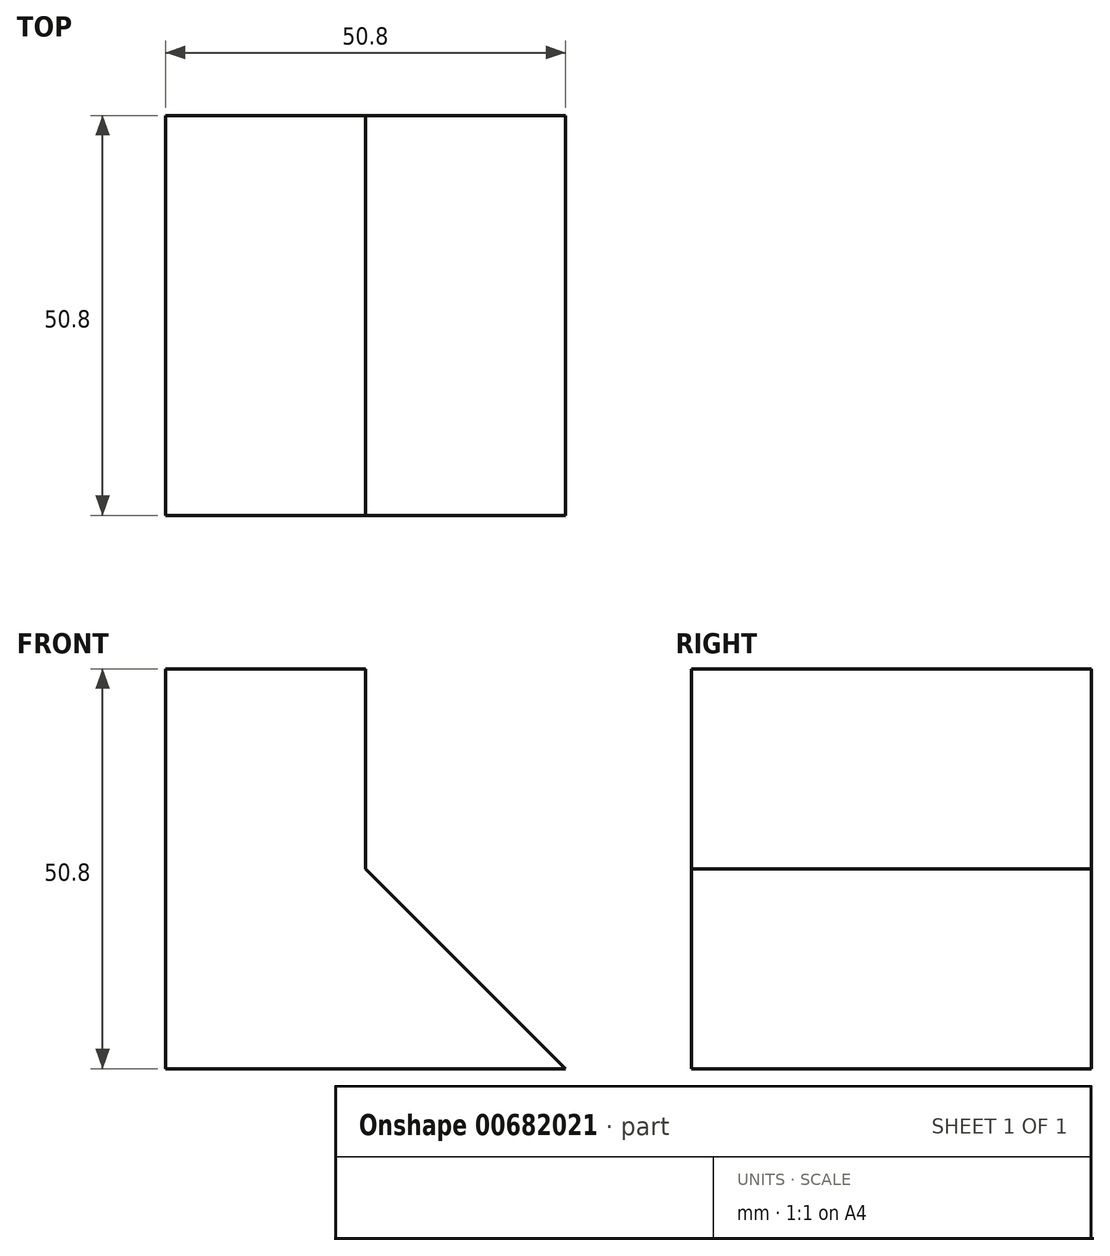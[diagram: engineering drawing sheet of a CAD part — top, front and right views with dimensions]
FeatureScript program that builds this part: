
annotation { "Feature Type Name" : "Feature", "Feature Type Description" : "" }
export const myFeature = defineFeature(function(context is Context, id is Id, definition is map)
    precondition{}
    {
        {
            var Q0;
            Q0=qCreatedBy(makeId("Front.planeOp"),FACE);
            var sketch = newSketch(context, id + "F0", { "sketchPlane" : qUnion([Q0])});
            skLineSegment(sketch, "E0", {"start": v(0.12, 10.32) * mm, "end": v(-50.68, 10.32) * mm});
            skLineSegment(sketch, "E1", {"start": v(-50.68, 10.32) * mm, "end": v(-50.68, 61.12) * mm});
            skLineSegment(sketch, "E2", {"start": v(-50.68, 61.12) * mm, "end": v(-25.28, 61.12) * mm});
            skLineSegment(sketch, "E3", {"start": v(-25.28, 61.12) * mm, "end": v(-25.28, 35.72) * mm});
            skLineSegment(sketch, "E4", {"start": v(-25.28, 35.72) * mm, "end": v(0.12, 10.32) * mm});
            skSolve(sketch);
        }
        {
            var Q0;
            Q0 = qSketchRegion(id + "F0", true);
            extrude(context, id + "F1", {"entities" : qUnion([Q0]), "depth" : 50.8 * mm, "offsetDistance" : 25.4 * mm});
        }
    });
